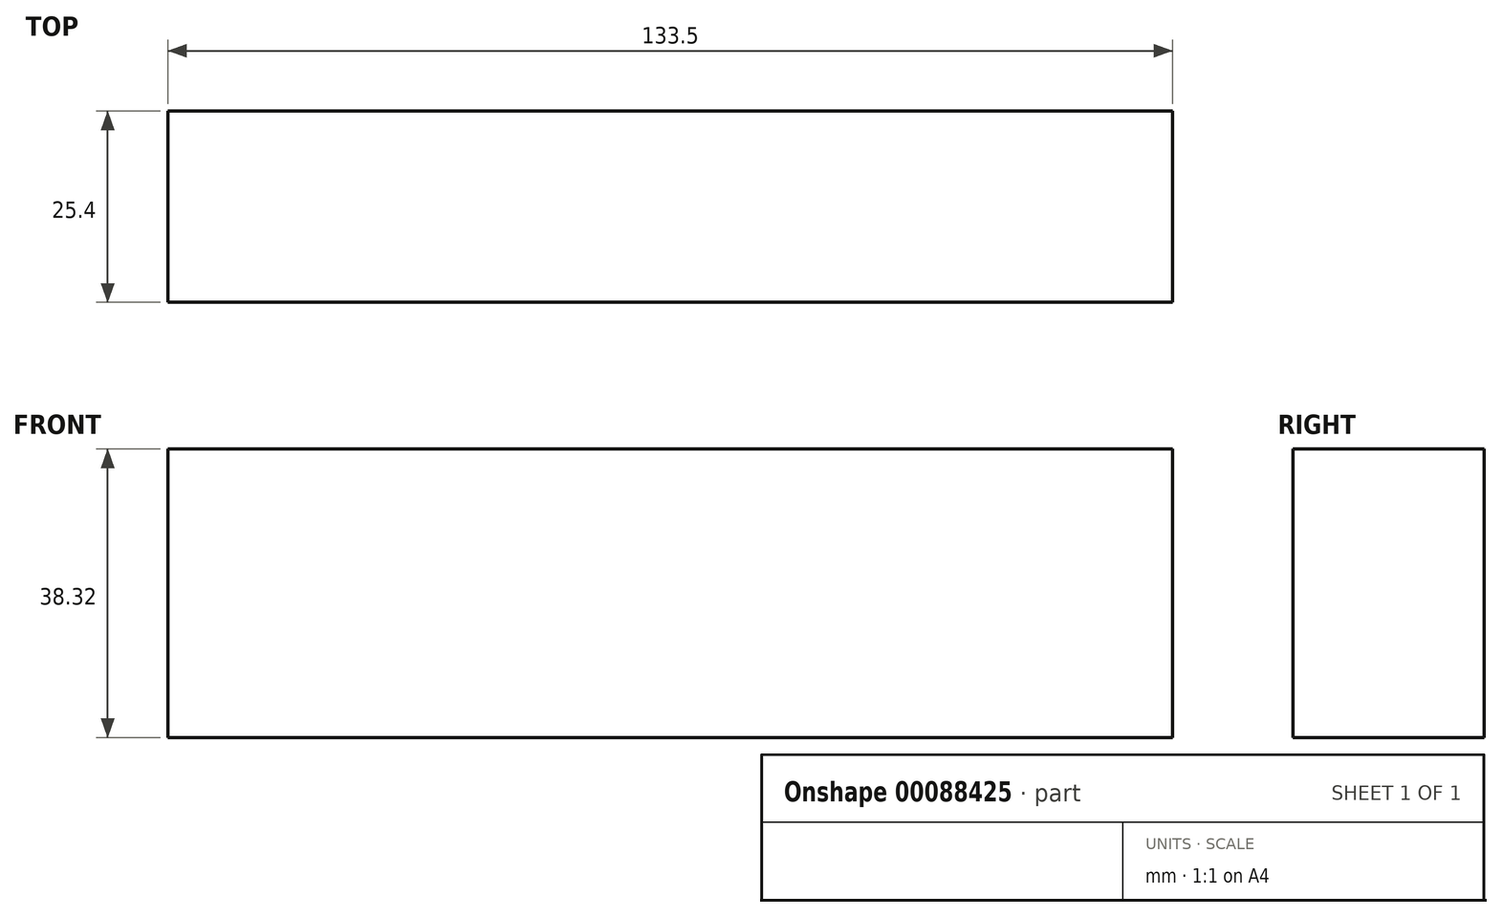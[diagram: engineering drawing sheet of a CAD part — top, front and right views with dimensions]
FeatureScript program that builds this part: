
annotation { "Feature Type Name" : "Feature", "Feature Type Description" : "" }
export const myFeature = defineFeature(function(context is Context, id is Id, definition is map)
    precondition{}
    {
        {
            var Q0;
            Q0=qCreatedBy(makeId("Front.planeOp"),FACE);
            var sketch = newSketch(context, id + "F0", { "sketchPlane" : qUnion([Q0])});
            skLineSegment(sketch, "E0.bottom", {"start": v(-119.68, 42.82) * mm, "end": v(13.82, 42.82) * mm});
            skLineSegment(sketch, "E0.top", {"start": v(-119.68, 4.5) * mm, "end": v(13.82, 4.5) * mm});
            skLineSegment(sketch, "E0.left", {"start": v(-119.68, 42.82) * mm, "end": v(-119.68, 4.5) * mm});
            skLineSegment(sketch, "E0.right", {"start": v(13.82, 42.82) * mm, "end": v(13.82, 4.5) * mm});
            skSolve(sketch);
        }
        {
            var Q0;
            Q0=makeQuery(id+"F0.imprint","IMPRINT",FACE,{"disambiguationData":[TD([[makeQuery(id+"F0.imprint","IMPRINT",EDGE,{"derivedFrom":sQuery(id+"F0.wireOp",EDGE,"E0.bottom")}),-1.0]])]});
            extrude(context, id + "F1", {"entities" : qUnion([Q0]), "depth" : 25.4 * mm});
        }
    });
